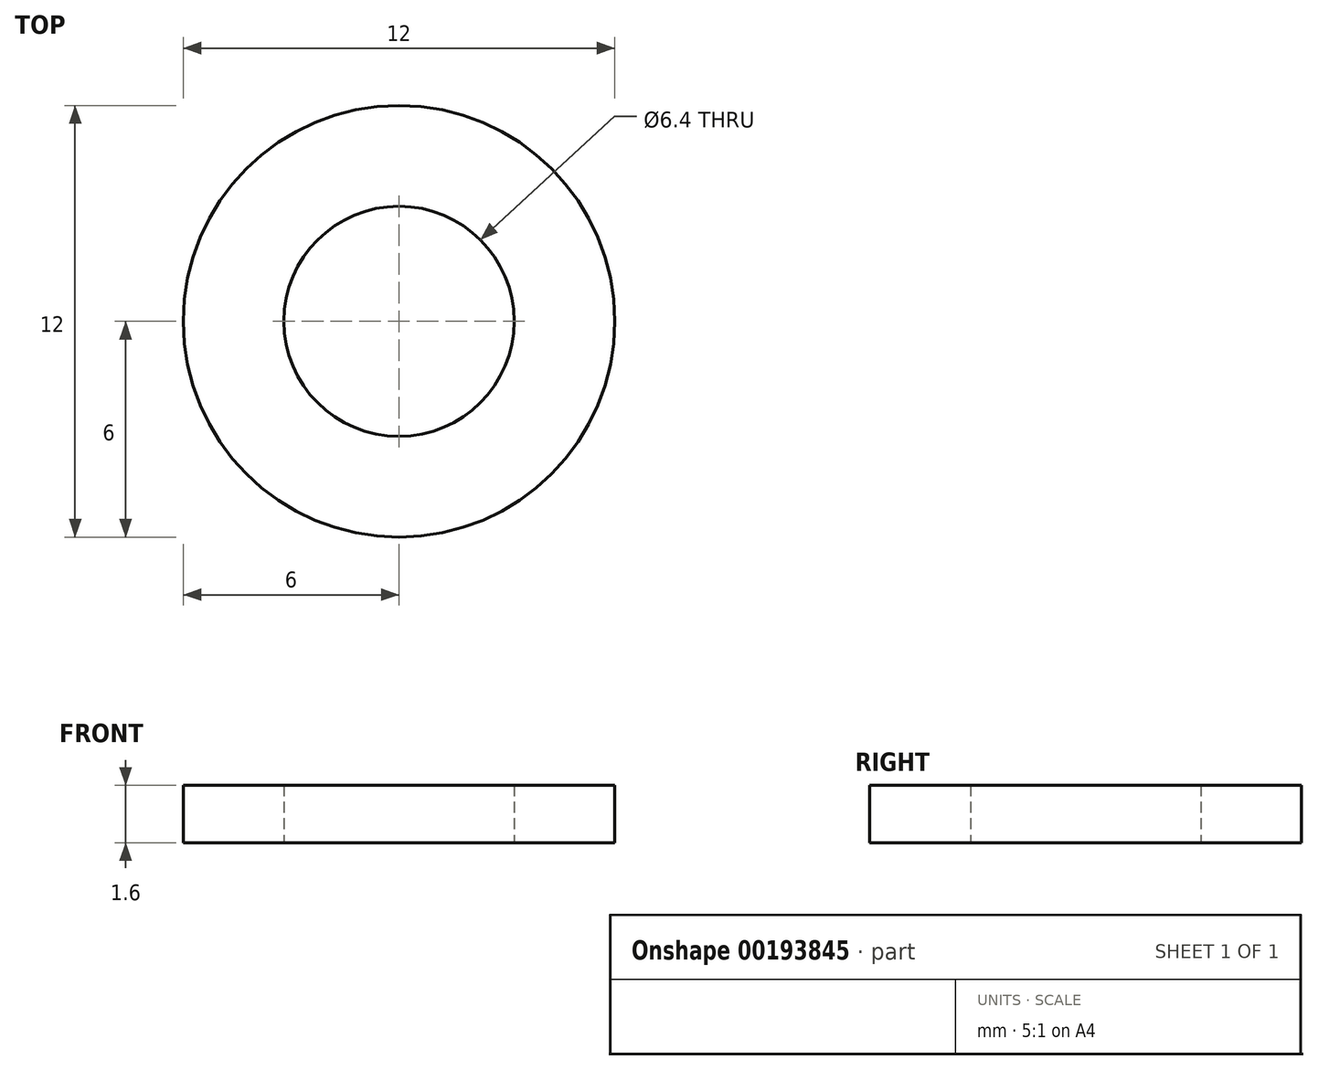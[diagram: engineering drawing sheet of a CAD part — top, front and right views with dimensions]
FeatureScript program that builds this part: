
annotation { "Feature Type Name" : "Feature", "Feature Type Description" : "" }
export const myFeature = defineFeature(function(context is Context, id is Id, definition is map)
    precondition{}
    {
        {
            var Q0;
            Q0=qCreatedBy(makeId("Top.planeOp"),FACE);
            var sketch = newSketch(context, id + "F0", { "sketchPlane" : qUnion([Q0])});
            skCircle(sketch, "E0", {"center": v(0, 0) * mm, "radius": 6 * mm});
            skCircle(sketch, "E1", {"center": v(0, 0) * mm, "radius": 3.2 * mm});
            skSolve(sketch);
        }
        {
            var Q0;
            Q0=makeQuery(id+"F0.imprint","IMPRINT",FACE,{"disambiguationData":[TD([[makeQuery(id+"F0.imprint","IMPRINT",EDGE,{"derivedFrom":sQuery(id+"F0.wireOp",EDGE,"E0")}),1.0]])]});
            extrude(context, id + "F1", {"entities" : qUnion([Q0]), "depth" : 1.6 * mm});
        }
    });
